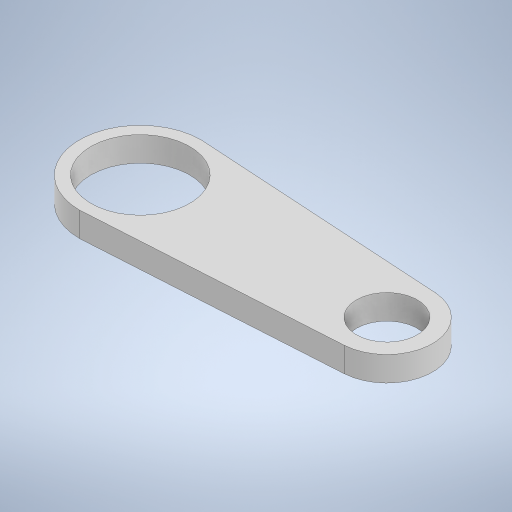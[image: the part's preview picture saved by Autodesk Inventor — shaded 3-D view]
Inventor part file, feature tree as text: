
AUTODESK INVENTOR PART (.ipt)
format: ipt  version: 2024 (Build 280153000, 153)  size: 249,344 bytes
history: native  units: mm
features: extrude x1, sketch x1
ambient origin geometry x8: Origin, YZ Plane, XZ Plane, XY Plane, X Axis, Y Axis, Z Axis, Center Point
bodies: Solid1 (feature_tree)
feature tree (2):
  extrude  "Extrusion1"  Depth=32.456mm
  sketch  "Sketch1"  dims[d0=13.0mm d1=32.456mm d2=8.0mm d3=16.0mm d4=12.0mm d5=3.25mm d6=0.0mm]
